# Revit family: IS_iLifeB_T4608_BIM_NL
name_source: partatom
category: Plumbing Fixtures
units: mm (PartAtom-declared; Revit-internal decimal feet)

## family parameters
Always vertical = No
Cut with Voids When Loaded = No
OmniClass Number = 23.45.05.14.14
OmniClass Title = Sinks/Lavatories
Part Type = Normal
Room Calculation Point = No
Round Connector Dimension = Use Diameter
Shared = No
Work Plane-Based = No

## types (2) — shared parameters
Accesoires = https://www.idealstandard.nl
Accessories = https://www.idealstandard.nl
Afmetingen = 550 x 440 x 180 mm
AfstandsEenheid = Millimeter
Afwerking = Weiß
AreaMeasurement = Internal
AreaUnits = Millimetres
BIMObjectName = IS_IdealStandard_Wall-hungwashbasins_i.lifeB_T4608
BIMobject category = Wash Basins
BIMobject category code = wash-basins
BIMobject main category = Sanitary
BIMobject main category code = sanitary
Beschrijvinggarantie = Herstellergarantie
BimObjectNaam = IS_IdealStandard_Wall-hungwashbasins_i.lifeB_T4608
Brand = Ideal Standard
Brand url = https://www.idealstandard.nl
Breedte = 549.293549
Category = Sanitary
Classification = Washbasin
ConnectionType = Plumbing
CurrencyUnit = €
CurrentRevision = 1
Date of publishing = 22/07/2022
Diepte = 440 mm
DurationUnit = Years
DuurEenheid = Jahre
Edition number = 1
ElementType = Fixed
ExpectedLife = 99
GTIN code = https://8014140503705
Garantieonderdelen = 5
Garantieunits = Jahre
GemaaktOp = 22/07/2022
Help = https://www.idealstandard.nl
Hoogte = 180.0227
Hulp = https://www.idealstandard.nl
IFC Classification = Sanitary Terminal
IfcExportAs = IfcSanitaryTerminalType
IfcExportType = WASHHANDBASIN
Installatieinstructies = https://www.idealstandard.nl
Installation instructions = https://www.idealstandard.nl
InstallationInstructions = https://www.idealstandard.nl
Kleur = Weiß
Lengte = 440 mm
LinearUnits = millimitres
MaintenanceInformation = https://www.idealstandard.nl
Manufacturer = Ideal Standard
Manufacturer name = Ideal Standard
ManufacturerURL = https://www.idealstandard.nl
Materiaal = Schamotte
Material = Fireclay
Material main = Fireclay
Merk = Ideal Standard
ModelReference = Ideal Standard i.life B  basin 55 cm with center taphole and overflow
NBS Reference Code = 45-35-70/368
NBS Reference Description = Wall hung hand rinse basins
Name = Wall-hungwashbasins_i.lifeB_T4608_IdealStandard
NettWeight = 15.3
Nettogewicht = 15.3
NominalDepth = 440 mm
NominalHeight = 180 mm
NominalLength = 440 mm
NominalWidth = 549 mm
OmniClass Code = 23-39 29 13 21 19
OmniClass Description = Surface Water Retention Basins
OppervlakteEenheid = Millimeter
PredefinedType = Washbasin
Product Guid = ed2385bd-e552-41aa-b28f-e8589424c53a
Product SKU = T4608
Product certification = https://www.idealstandard.nl
Product data url = https://bimobject.com
Product family = Washbasin
Product group = Sanitary
Product name = I.Life b basin 55 cm with center taphole
Product url = https://www.idealstandard.nl
ProductInformation = https://www.idealstandard.nl
Productinformatie = https://www.idealstandard.nl
QR code = http://bimobject.com
Referentie = Ideal Standard i.life B  basin 55 cm with center taphole and overflow
Revisie = 1
Shape = Sculptured
Size = 550 x 440 x 180 mm
Space = Internal
SpareParts = https://www.idealstandard.nl
Technical description = https://www.idealstandard.nl
Telefoonnummer = 077 355 08 08
Toepassing = Waschbecken
Typeconnectie = Installation
Typewastafel = wandhängendes Waschbecken
UNSPSC Code = 301815
URL = https://www.idealstandard.nl
Uniclass 2015 Code = Pr_40_20_96_96
Uniclass 2015 Name = Wall-hung washbasins
Uniclass2015Beschrijving = Wall-hung washbasins
Uniclass2015Code = Pr_40_20_96_96
Uniclass2015Referentie = Pr_40_20_96_96
Uniclass2015Title = Wall-hung washbasins
Uniclass2015Version = v1.26
Urlproducent = https://www.idealstandard.nl
ValutaEenheid = Euro
Versie = 1
Version = 1
Verwachtelevensduur = 5
VolumeUnits = Liters
Volumeunits = Liter
Vorm = Skulptur
WRASURL = https://www.wrasapprovals.co.uk
WarrantyDescription = manufacturer warranty
WarrantyDurationUnit = years
WashHandBasinMounting = Wall hung
WashHandBasinType = Wall Hung washbasin
Weight Net (Kg) = 44
Wisselstukken = https://www.idealstandard.nl
Youtube clip = https://www.youtube.com
zero-valued in all types: BrutoGewicht, Vervangingskosten

## per-type parameters (varying)
| type | Artikelnummer | Artikelomschrijving | Artikelreferentie | BarCode | Color | Description | Eigenschappen | Features | Finish | MainColor | Model | ModelNumber |
| T460801 - Ideal Standard i.life B  basin 55 cm with center taphole and overflow - White Finish | T460801 | Ideal Standard i.life B Waschtisch 55 cm mit Hahnlochmitte, mit Überlauf, weiß, im Karton, EU-Palette | T460801 | 8014140503705 | White | Ideal Standard i.life B  basin 55 cm with center taphole, with overflow, white, in carton box, EU pallet | Becken 55 cm mit Hahnlochmitte, mit Überlauf, weiß, im Karton, EU-Palette | basin 55 cm with center taphole, with overflow, white, in carton box, EU pallet | White | White | T460801 | T460801 |
| T4608MA - Ideal Standard i.life B  basin 55 cm with center taphole and overflow  - Ideal Plus White | T4608MA | Ideal Standard i.life B Waschtisch 55 cm mit Hahnlochmitte, mit Überlauf, weiß Ideal Plus, im Karton, EU-Palette | T4608MA | 8014140506720 | Ideal Plus White | Ideal Standard i.life B  basin 55 cm with center taphole, with overflow, white Ideal Plus, in carton box, EU pallet | Waschtisch 55 cm mit Hahnlochmitte, mit Überlauf, weiß Ideal Plus, im Karton, EU-Palette | basin 55 cm with center taphole, with overflow, white Ideal Plus, in carton box, EU pallet | Ideal Plus White | Ideal Plus White | T4608MA | T4608MA |

## geometry (parser evidence)
native form markers: Sweep x3
no freeform markers — native parametric forms only
